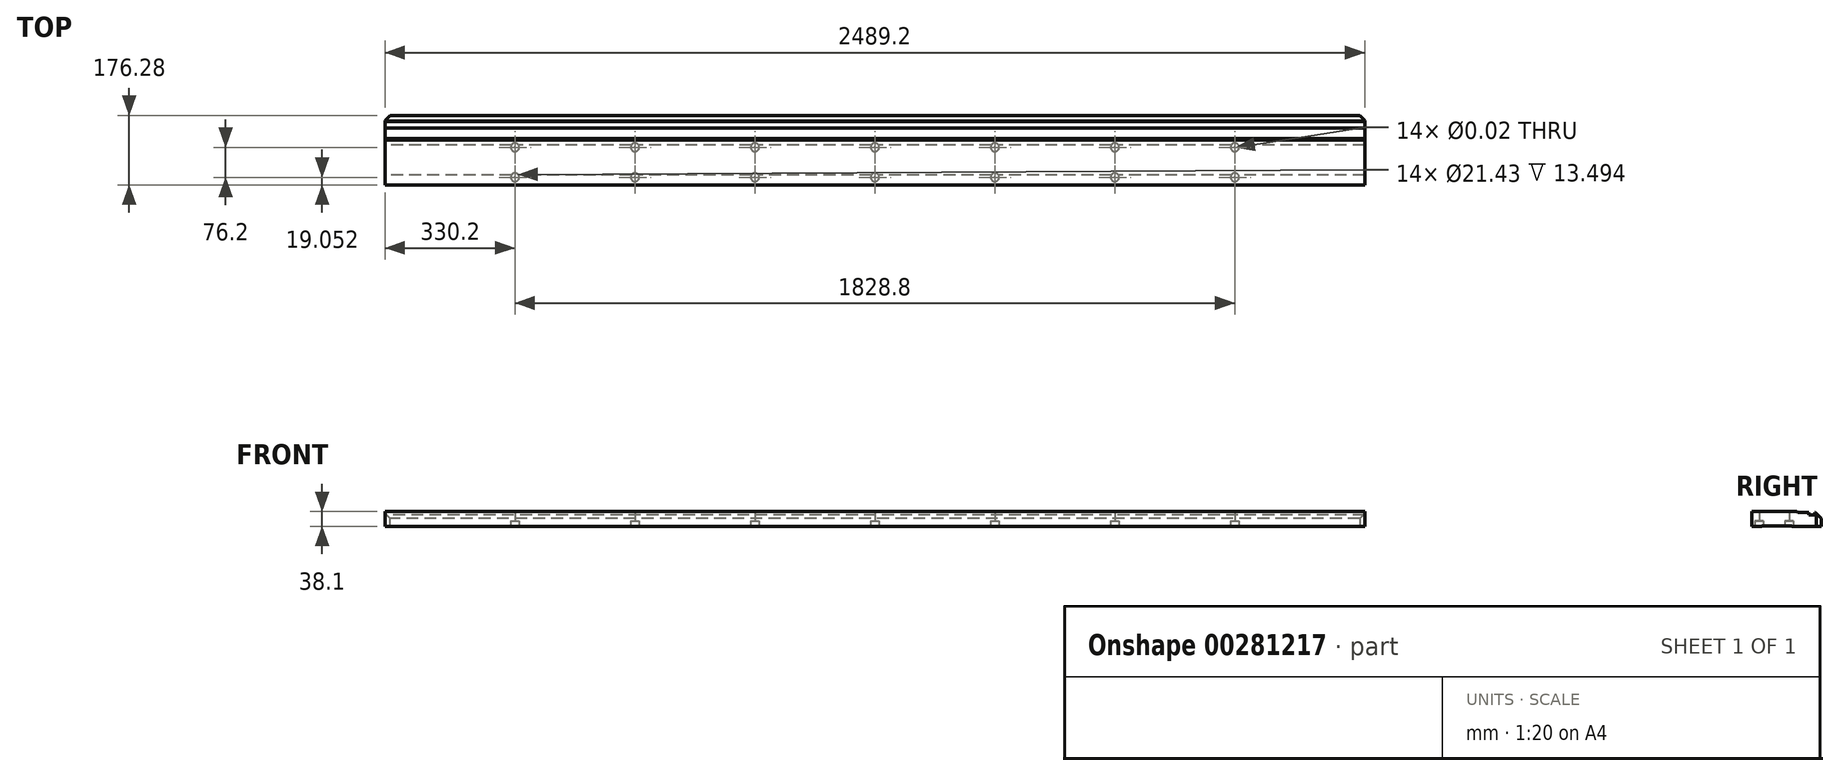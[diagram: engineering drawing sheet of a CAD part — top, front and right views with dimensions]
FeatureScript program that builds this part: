
annotation { "Feature Type Name" : "Feature", "Feature Type Description" : "" }
export const myFeature = defineFeature(function(context is Context, id is Id, definition is map)
    precondition{}
    {
        {
            var Q0;
            Q0=qCreatedBy(makeId("Right.planeOp"),FACE);
            var sketch = newSketch(context, id + "F0", { "sketchPlane" : qUnion([Q0])});
            skLineSegment(sketch, "E0.bottom", {"start": v(-88.14, 19.05) * mm, "end": v(26.16, 19.05) * mm});
            skLineSegment(sketch, "E0.top", {"start": v(-88.14, -19.05) * mm, "end": v(-62.74, -19.05) * mm});
            skLineSegment(sketch, "E0.left", {"start": v(-88.14, 19.05) * mm, "end": v(-88.14, -19.05) * mm});
            skPoint(sketch, "E0.middle", {"position": v(0, 0) * mm});
            skLineSegment(sketch, "E1.0", {"start": v(-62.74, 19.05) * mm, "end": v(-62.74, -19.05) * mm, "construction": true});
            skLineSegment(sketch, "E2.top", {"start": v(-62.74, -17.53) * mm, "end": v(13.46, -17.53) * mm});
            skLineSegment(sketch, "E2.left", {"start": v(-62.74, -19.05) * mm, "end": v(-62.74, -17.53) * mm});
            skLineSegment(sketch, "E2.right", {"start": v(13.46, -19.05) * mm, "end": v(13.46, -17.53) * mm});
            skLineSegment(sketch, "E3.trimOffspring", {"start": v(13.46, -19.05) * mm, "end": v(88.14, -19.05) * mm});
            skLineSegment(sketch, "E4.0", {"start": v(26.16, 19.05) * mm, "end": v(26.16, -19.05) * mm, "construction": true});
            skLineSegment(sketch, "E5", {"start": v(26.16, 19.05) * mm, "end": v(29.21, 16) * mm});
            skLineSegment(sketch, "E6", {"start": v(29.21, 16) * mm, "end": v(56.39, 16) * mm});
            skLineSegment(sketch, "E7.0", {"start": v(13.46, 1.52) * mm, "end": v(88.14, 1.52) * mm});
            skLineSegment(sketch, "E8", {"start": v(88.14, 1.52) * mm, "end": v(73.66, 16) * mm});
            skLineSegment(sketch, "E9.0", {"start": v(73.91, 1.52) * mm, "end": v(73.91, -19.05) * mm});
            skLineSegment(sketch, "E10.0", {"start": v(64.26, 19.05) * mm, "end": v(64.26, -19.05) * mm, "construction": true});
            skLineSegment(sketch, "E11.0", {"start": v(56.39, 16) * mm, "end": v(56.39, 9.65) * mm});
            skLineSegment(sketch, "E12.0", {"start": v(56.39, 9.65) * mm, "end": v(72.14, 9.65) * mm});
            skLineSegment(sketch, "E13.trimOffspring", {"start": v(72.14, 16) * mm, "end": v(73.66, 16) * mm});
            skLineSegment(sketch, "E14.MirrorCS", {"start": v(72.14, 16) * mm, "end": v(72.14, 9.65) * mm});
            skLineSegment(sketch, "E15.trimOffspring", {"start": v(88.14, 1.52) * mm, "end": v(88.14, -19.05) * mm});
            skPoint(sketch, "E16.orphan", {"position": v(88.14, 19.05) * mm});
            skLineSegment(sketch, "E17.trimOffspring", {"start": v(70.61, 19.05) * mm, "end": v(51.5, 38.16) * mm});
            skLineSegment(sketch, "E18.trimOffspring", {"start": v(64.26, 19.05) * mm, "end": v(70.61, 19.05) * mm});
            skSolve(sketch);
        }
        {
            var Q0;
            Q0 = qSketchRegion(id + "F0", true);
            extrude(context, id + "F1", {"entities" : qUnion([Q0]), "endBound" : BoundingType.SYMMETRIC, "depth" : 2489.2 * mm});
        }
        {
            var Q0;
            Q0=makeQuery(id+"F1.opExtrude","SWEPT_FACE",FACE,{"disambiguationData":[OSD([sQuery(id+"F0.wireOp",EDGE,"E3.trimOffspring")])]});
            var sketch = newSketch(context, id + "F2", { "sketchPlane" : qUnion([Q0])});
            skLineSegment(sketch, "E19", {"start": v(0, -273.83) * mm, "end": v(0, 196.28) * mm, "construction": true});
            skLineSegment(sketch, "E20.0", {"start": v(939.8, 69.09) * mm, "end": v(-939.8, 69.09) * mm, "construction": true});
            skLineSegment(sketch, "E21.0", {"start": v(939.8, -7.11) * mm, "end": v(-939.8, -7.11) * mm, "construction": true});
            skLineSegment(sketch, "E22.0", {"start": v(304.8, -273.83) * mm, "end": v(304.8, 196.28) * mm, "construction": true});
            skLineSegment(sketch, "E23.0", {"start": v(609.6, -273.83) * mm, "end": v(609.6, 196.28) * mm, "construction": true});
            skLineSegment(sketch, "E24.0", {"start": v(914.4, -273.83) * mm, "end": v(914.4, 196.28) * mm, "construction": true});
            skPoint(sketch, "E25", {"position": v(914.4, -7.11) * mm});
            skPoint(sketch, "E26", {"position": v(914.4, 69.09) * mm});
            skPoint(sketch, "E27", {"position": v(609.6, 69.09) * mm});
            skPoint(sketch, "E28", {"position": v(609.6, -7.11) * mm});
            skPoint(sketch, "E29", {"position": v(304.8, -7.11) * mm});
            skPoint(sketch, "E30", {"position": v(304.8, 69.09) * mm});
            skPoint(sketch, "E31", {"position": v(0, -7.11) * mm});
            skPoint(sketch, "E32", {"position": v(0, 69.09) * mm});
            skPoint(sketch, "E33.MirrorP", {"position": v(-914.4, -7.11) * mm});
            skPoint(sketch, "E34.MirrorP", {"position": v(-914.4, 69.09) * mm});
            skPoint(sketch, "E35.MirrorP", {"position": v(-609.6, 69.09) * mm});
            skPoint(sketch, "E36.MirrorP", {"position": v(-304.8, -7.11) * mm});
            skPoint(sketch, "E37.MirrorP", {"position": v(-304.8, 69.09) * mm});
            skPoint(sketch, "E38.MirrorP", {"position": v(-609.6, -7.11) * mm});
            skSolve(sketch);
        }
        {
            var Q0;
            Q0=sQuery(id+"F2.wireOp",VERTEX,"E25");
            var Q1;
            Q1=sQuery(id+"F2.wireOp",VERTEX,"E26");
            var Q2;
            Q2=sQuery(id+"F2.wireOp",VERTEX,"E27");
            var Q3;
            Q3=sQuery(id+"F2.wireOp",VERTEX,"E28");
            var Q4;
            Q4=sQuery(id+"F2.wireOp",VERTEX,"E29");
            var Q5;
            Q5=sQuery(id+"F2.wireOp",VERTEX,"E30");
            var Q6;
            Q6=sQuery(id+"F2.wireOp",VERTEX,"E31");
            var Q7;
            Q7=sQuery(id+"F2.wireOp",VERTEX,"E32");
            var Q8;
            Q8=sQuery(id+"F2.wireOp",VERTEX,"E36.MirrorP");
            var Q9;
            Q9=sQuery(id+"F2.wireOp",VERTEX,"E37.MirrorP");
            var Q10;
            Q10=sQuery(id+"F2.wireOp",VERTEX,"E38.MirrorP");
            var Q11;
            Q11=sQuery(id+"F2.wireOp",VERTEX,"E35.MirrorP");
            var Q12;
            Q12=sQuery(id+"F2.wireOp",VERTEX,"E33.MirrorP");
            var Q13;
            Q13=sQuery(id+"F2.wireOp",VERTEX,"E34.MirrorP");
            var Q14;
            Q14=makeQuery(id+"F1.opExtrude","SWEPT_BODY",BODY,{"disambiguationData":[OSD([sQuery(id+"F0.wireOp",EDGE,"E0.bottom"),sQuery(id+"F0.wireOp",EDGE,"E0.top"),sQuery(id+"F0.wireOp",EDGE,"E0.left"),sQuery(id+"F0.wireOp",EDGE,"E2.top"),sQuery(id+"F0.wireOp",EDGE,"E2.left"),sQuery(id+"F0.wireOp",EDGE,"E2.right"),sQuery(id+"F0.wireOp",EDGE,"E3.trimOffspring"),sQuery(id+"F0.wireOp",EDGE,"E5"),sQuery(id+"F0.wireOp",EDGE,"E6"),sQuery(id+"F0.wireOp",EDGE,"E8"),sQuery(id+"F0.wireOp",EDGE,"E11.0"),sQuery(id+"F0.wireOp",EDGE,"E12.0"),sQuery(id+"F0.wireOp",EDGE,"E13.trimOffspring"),sQuery(id+"F0.wireOp",EDGE,"E14.MirrorCS"),sQuery(id+"F0.wireOp",EDGE,"E15.trimOffspring")])]});
            hole(context, id + "F3", {"style" : HoleStyle.C_BORE, "endStyle" : HoleEndStyle.THROUGH, "standardTappedOrClearance" : lookupTablePath({ "standard" : "ANSI", "size" : "9/16 (0.56)", "type" : "Drilled" }), "standardBlindInLast" : lookupTablePath({ "standard" : "ANSI", "size" : "9/16", "type" : "Drilled" }), "holeDiameter" : 9 / 406.4 * mm, "cBoreDiameter" : 21.43 * mm, "cBoreDepth" : 13.5 * mm, "tappedDepth" : 42.34 * mm, "tapClearance" : 3, "startFromSketch" : true, "locations" : qUnion([Q0, Q1, Q2, Q3, Q4, Q5, Q6, Q7, Q8, Q9, Q10, Q11, Q12, Q13]), "scope" : qUnion([Q14])});
        }
        {
            var Q0;
            Q0=makeQuery(id+"F1.opExtrude","CAP_EDGE",EDGE,{"disambiguationData":[OSD([sQuery(id+"F0.wireOp",EDGE,"E15.trimOffspring")])],"isStart":false});
            var Q1;
            Q1=makeQuery(id+"F1.opExtrude","CAP_EDGE",EDGE,{"disambiguationData":[OSD([sQuery(id+"F0.wireOp",EDGE,"E15.trimOffspring")])],"isStart":true});
            chamfer(context, id + "F4", {"entities" : qUnion([Q0, Q1]), "width" : 12.7 * mm, "tangentPropagation" : true});
        }
    });
